FCSTD DOCUMENT  (FreeCAD 0.16R)
Label: HeadLightBracketClamp
License: All rights reserved
LicenseURL: http://en.wikipedia.org/wiki/All_rights_reserved
objects: Sketcher::SketchObject×5, PartDesign::Pocket×4, PartDesign::Chamfer×2, PartDesign::Pad×1, Mesh::Feature×1
note: 17 computed .brp shape members not serialized (recipe doc carries the construction recipe); baked Part::Feature solids carry a one-line shape summary decoded from their .brp

FEATURE [Sketcher::SketchObject] Sketch
  sketch-geometry (4):
    g0: LineSegment StartX=-30 StartY=5 StartZ=0 EndX=30 EndY=5 EndZ=0
    g1: LineSegment StartX=30 StartY=5 StartZ=0 EndX=30 EndY=-5 EndZ=0
    g2: LineSegment StartX=30 StartY=-5 StartZ=0 EndX=-30 EndY=-5 EndZ=0
    g3: LineSegment StartX=-30 StartY=-5 StartZ=0 EndX=-30 EndY=5 EndZ=0
  constraints (11):
    c: Coincident(g0,g1)
    c: Coincident(g1,g2)
    c: Coincident(g2,g3)
    c: Coincident(g3,g0)
    c: Horizontal(g0)
    c: Horizontal(g2)
    c: Vertical(g1)
    c: Vertical(g3)
    c: Symmetric(g0,g1,g-1)
    c: Distance(g0) = 60
    c: Distance(g1) = 10
FEATURE [PartDesign::Pad] Pad
  Length = 25
  Length2 = 100
  Sketch = -> Sketch
  Type = 0
FEATURE [Sketcher::SketchObject] Sketch001
  ExternalGeometry = -> [Pad]
  Placement = pos=(0,5,0) rot=(0,0.707107,0.707107;3.14159rad)
  Support = -> Pad [Face1]
  sketch-geometry (1):
    g0: Circle CenterX=0 CenterY=-5 CenterZ=0 NormalX=0 NormalY=0 NormalZ=1 Radius=20.75
  constraints (3):
    c: Radius(g0) = 20.75
    c: PointOnObject(g0,g-2)
    c: DistanceY(g0) = -5
FEATURE [PartDesign::Pocket] Pocket
  Length = 5
  Sketch = -> Sketch001
  Type = 1
FEATURE [Sketcher::SketchObject] Sketch002
  ExternalGeometry = -> [Pocket]
  Placement = pos=(0,0,0) rot=(1,0,0;3.14159rad)
  Support = -> Pocket [Face4]
  sketch-geometry (2):
    g0: Circle CenterX=-25 CenterY=0 CenterZ=0 NormalX=0 NormalY=0 NormalZ=1 Radius=2.2
    g1: Circle CenterX=25 CenterY=0 CenterZ=0 NormalX=0 NormalY=0 NormalZ=1 Radius=2.2
  constraints (6):
    c: PointOnObject(g0,g-1)
    c: PointOnObject(g1,g-1)
    c: Radius(g1) = 2.2
    c: Equal(g1,g0)
    c: DistanceX(g-1,g1) = 25
    c: DistanceX(g0,g-1) = 25
FEATURE [PartDesign::Pocket] Pocket001
  Length = 5
  Sketch = -> Sketch002
  Type = 1
FEATURE [Sketcher::SketchObject] Sketch003
  ExternalGeometry = -> [Pocket001]
  Placement = pos=(0,0,25) rot=(0,0,1;0rad)
  Support = -> Pocket001 [Face6]
  sketch-geometry (2):
    g0: Circle CenterX=-25 CenterY=0 CenterZ=0 NormalX=0 NormalY=0 NormalZ=1 Radius=4
    g1: Circle CenterX=25 CenterY=0 CenterZ=0 NormalX=0 NormalY=0 NormalZ=1 Radius=4
  constraints (4):
    c: Radius(g1) = 4
    c: Equal(g1,g0)
    c: Coincident(g0,g-3)
    c: Coincident(g1,g-4)
FEATURE [PartDesign::Pocket] Pocket002
  Length = 11
  Sketch = -> Sketch003
  Type = 0
FEATURE [Sketcher::SketchObject] Sketch004
  Placement = pos=(0,-5,0) rot=(1,0,0;1.5708rad)
  Support = -> Pocket002 [Face8]
  sketch-geometry (5):
    g0: LineSegment StartX=0 StartY=40 StartZ=0 EndX=-45 EndY=0 EndZ=0
    g1: LineSegment StartX=-45 StartY=0 StartZ=0 EndX=-45 EndY=50 EndZ=0
    g2: LineSegment StartX=-45 StartY=50 StartZ=0 EndX=45 EndY=50 EndZ=0
    g3: LineSegment StartX=45 StartY=50 StartZ=0 EndX=45 EndY=0 EndZ=0
    g4: LineSegment StartX=45 StartY=0 StartZ=0 EndX=0 EndY=40 EndZ=0
  constraints (14):
    c: Coincident(g0,g1)
    c: Coincident(g1,g2)
    c: Horizontal(g2)
    c: Coincident(g2,g3)
    c: Coincident(g3,g4)
    c: Coincident(g4,g0)
    c: PointOnObject(g0,g-2)
    c: Symmetric(g0,g3,g-1)
    c: DistanceY(g0) = 40
    c: Equal(g1,g3)
    c: Vertical(g1)
    c: Vertical(g3)
    c: Distance(g1) = 50
    c: DistanceX(g2,g2) = 90
FEATURE [PartDesign::Pocket] Pocket003
  Length = 5
  Sketch = -> Sketch004
  Type = 1
FEATURE [PartDesign::Chamfer] Chamfer
  Base = -> Pocket003 [Edge1,Edge2,Edge3,Edge4,Edge5,Edge6,Edge7,Edge8,Edge15,Edge14,Edge10,Edge28,Edge25,Edge24,Edge20,Edge18]
  Size = 1
FEATURE [PartDesign::Chamfer] Chamfer001
  Base = -> Chamfer [Edge34,Edge40,Edge42,Edge30]
  Size = 1
FEATURE [Mesh::Feature] Mesh  label="Chamfer001 (Meshed)"
